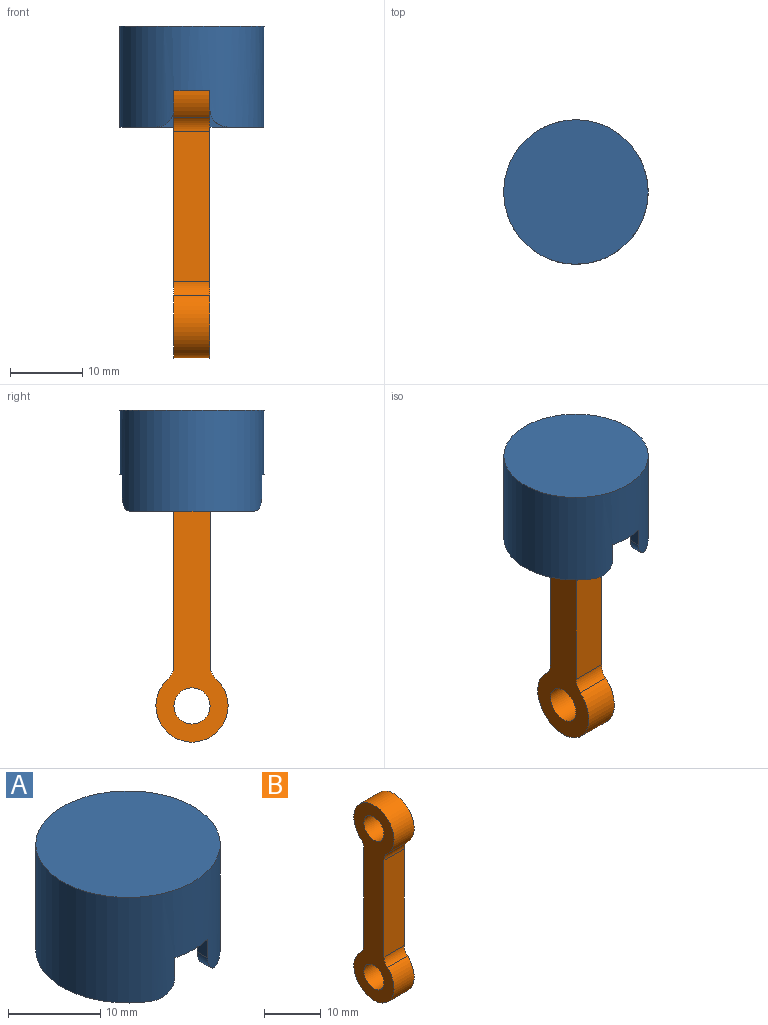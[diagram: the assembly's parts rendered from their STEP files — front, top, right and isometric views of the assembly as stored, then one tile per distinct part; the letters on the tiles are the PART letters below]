
ASSEMBLY  parts=2 mates=1
PART A: 23 faces, bbox 20x20x14 mm
  f0: cylinder r=10mm len=20mm, axis (0,0,-1), area 823.5mm2, adj f1,f2,f3,f9,f10,f11,f15,f16
  f1: plane 20x20mm, normal (0,0,1), area 314.2mm2, adj f0
  f2: plane 2.5x1.56mm, normal (1,0,0), area 3.9mm2, adj f0,f8,f16,f19
  f3: plane 2.5x1.56mm, normal (1,0,0), area 3.9mm2, adj f0,f4,f17,f20
  f4: cylinder r=8.5mm len=16.25mm, axis (0,0,-1), area 188mm2, adj f3,f5,f9,f10,f14,f15,f17,f18
  f5: plane 10x5.62mm, normal (0,-1,0), area 56.2mm2, adj f4,f6,f9,f18
  f6: plane 10x5mm, normal (1,0,0), area 50mm2, adj f5,f7,f9,f18
  f7: plane 10x5.62mm, normal (0,1,0), area 56.2mm2, adj f6,f8,f9,f18
  f8: cylinder r=8.5mm len=16.25mm, axis (0,0,-1), area 188mm2, adj f2,f7,f9,f11,f12,f15,f16,f18
  f9: plane 17.32x7.5mm, normal (0,0,-1), area 57.1mm2, adj f0,f4,f5,f6,f7,f8,f19,f20
  f10: plane 2.5x1.56mm, normal (-1,0,0), area 3.9mm2, adj f0,f4,f17,f22
  f11: plane 2.5x1.56mm, normal (-1,0,0), area 3.9mm2, adj f0,f8,f16,f21
  f12: plane 10x5.62mm, normal (0,1,0), area 56.2mm2, adj f8,f13,f15,f18
  f13: plane 10x5mm, normal (-1,0,0), area 50mm2, adj f12,f14,f15,f18
  f14: plane 10x5.62mm, normal (0,-1,0), area 56.2mm2, adj f4,f13,f15,f18
  f15: plane 17.32x7.5mm, normal (0,0,-1), area 57.1mm2, adj f0,f4,f8,f12,f13,f14,f21,f22
  f16: plane 5x1.88mm, normal (0,0,-1), area 7.6mm2, adj f0,f2,f8,f11
  f17: plane 5x1.88mm, normal (0,0,-1), area 7.6mm2, adj f0,f3,f4,f10
  f18: plane 17x16.25mm, normal (0,0,-1), area 168.2mm2, adj f4,f5,f6,f7,f8,f12,f13,f14
  f19: cylinder r=2.5mm len=2.81mm, axis (0,1,0), area 6.4mm2, adj f0,f2,f8,f9
  f20: cylinder r=2.5mm len=2.81mm, axis (0,1,0), area 6.4mm2, adj f0,f3,f4,f9
  f21: cylinder r=2.5mm len=2.81mm, axis (0,-1,0), area 6.4mm2, adj f0,f8,f11,f15
  f22: cylinder r=2.5mm len=2.81mm, axis (0,-1,0), area 6.4mm2, adj f0,f4,f10,f15
PART B: 12 faces, bbox 5x10x42 mm
  f0: cylinder r=2.5mm len=5mm, axis (-1,0,0), area 10.5mm2, adj f1,f8,f10,f11
  f1: plane 20.82x5mm, normal (0,-1,0), area 104.1mm2, adj f0,f2,f10,f11
  f2: cylinder r=2.5mm len=5mm, axis (-1,0,0), area 10.5mm2, adj f1,f3,f10,f11
  f3: cylinder r=5mm len=10mm, axis (-1,0,0), area 120.6mm2, adj f2,f4,f10,f11
  f4: cylinder r=2.5mm len=5mm, axis (-1,0,0), area 10.5mm2, adj f3,f5,f10,f11
  f5: plane 20.82x5mm, normal (0,1,0), area 104.1mm2, adj f4,f6,f10,f11
  f6: cylinder r=2.5mm len=5mm, axis (-1,0,0), area 10.5mm2, adj f5,f8,f10,f11
  f7: cylinder r=2.5mm len=5mm, axis (-1,0,0), area 78.5mm2, adj f10,f11
  f8: cylinder r=5mm len=10mm, axis (-1,0,0), area 120.6mm2, adj f0,f6,f10,f11
  f9: cylinder r=2.5mm len=5mm, axis (-1,0,0), area 78.5mm2, adj f10,f11
  f10: plane 42x10mm, normal (1,0,0), area 230.8mm2, adj f0,f1,f2,f3,f4,f5,f6,f7
  f11: plane 42x10mm, normal (-1,0,0), area 230.8mm2, adj f0,f1,f2,f3,f4,f5,f6,f7
PLACE A at identity
PLACE B t=(0,0,10)mm
MATE revolute B.f9 <-> A.f13  axis (1,0,0) through (2.5,0,16)mm
